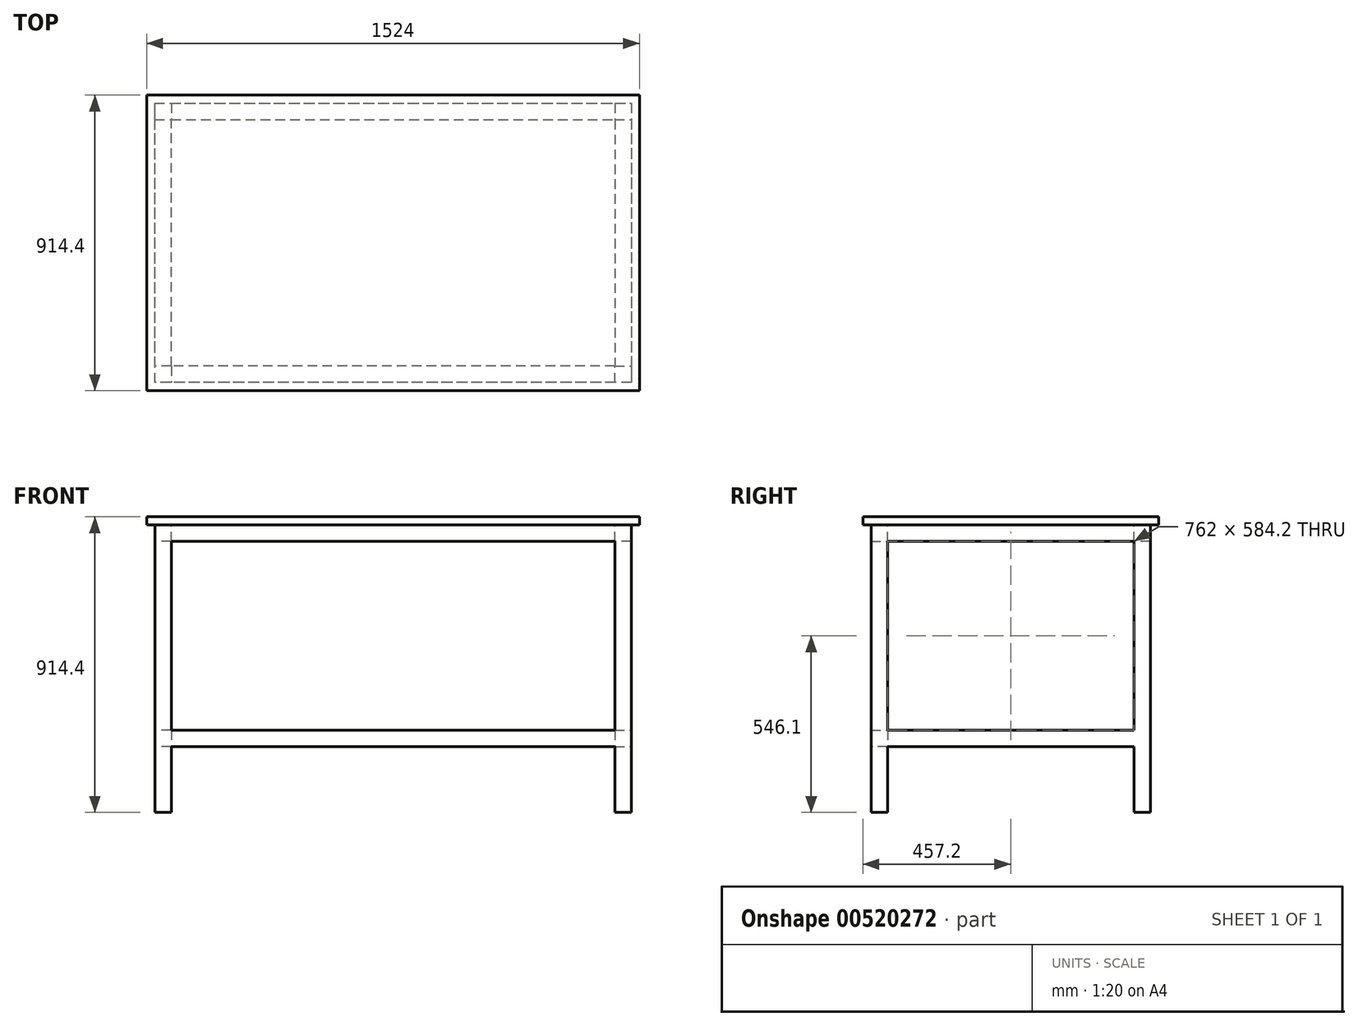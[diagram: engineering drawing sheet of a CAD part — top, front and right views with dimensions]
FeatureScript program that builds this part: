
annotation { "Feature Type Name" : "Feature", "Feature Type Description" : "" }
export const myFeature = defineFeature(function(context is Context, id is Id, definition is map)
    precondition{}
    {
        {
            var Q0;
            Q0=qCreatedBy(makeId("Top.planeOp"),FACE);
            var sketch = newSketch(context, id + "F0", { "sketchPlane" : qUnion([Q0])});
            skLineSegment(sketch, "E0.bottom", {"start": v(762, 457.2) * mm, "end": v(-762, 457.2) * mm});
            skLineSegment(sketch, "E0.top", {"start": v(762, -457.2) * mm, "end": v(-762, -457.2) * mm});
            skLineSegment(sketch, "E0.left", {"start": v(762, 457.2) * mm, "end": v(762, -457.2) * mm});
            skLineSegment(sketch, "E0.right", {"start": v(-762, 457.2) * mm, "end": v(-762, -457.2) * mm});
            skPoint(sketch, "E0.middle", {"position": v(0, 0) * mm});
            skSolve(sketch);
        }
        {
            var Q0;
            Q0 = qSketchRegion(id + "F0", true);
            extrude(context, id + "F1", {"entities" : qUnion([Q0]), "depth" : -25.4 * mm, "offsetDistance" : 25.4 * mm});
        }
        {
            var Q0;
            Q0=makeQuery(id+"F1.opExtrude","CAP_FACE",FACE,{"disambiguationData":[OSD([sQuery(id+"F0.wireOp",EDGE,"E0.bottom"),sQuery(id+"F0.wireOp",EDGE,"E0.top"),sQuery(id+"F0.wireOp",EDGE,"E0.left"),sQuery(id+"F0.wireOp",EDGE,"E0.right")])],"isStart":false});
            var sketch = newSketch(context, id + "F2", { "sketchPlane" : qUnion([Q0])});
            skLineSegment(sketch, "E1.0", {"start": v(736.6, 431.8) * mm, "end": v(-736.6, 431.8) * mm});
            skLineSegment(sketch, "E1.1", {"start": v(736.6, -431.8) * mm, "end": v(736.6, 431.8) * mm});
            skLineSegment(sketch, "E1.2", {"start": v(-736.6, -431.8) * mm, "end": v(736.6, -431.8) * mm});
            skLineSegment(sketch, "E1.3", {"start": v(-736.6, 431.8) * mm, "end": v(-736.6, -431.8) * mm});
            skLineSegment(sketch, "E2.0", {"start": v(685.8, 381) * mm, "end": v(-685.8, 381) * mm});
            skLineSegment(sketch, "E2.1", {"start": v(685.8, -381) * mm, "end": v(685.8, 381) * mm});
            skLineSegment(sketch, "E2.2", {"start": v(-685.8, -381) * mm, "end": v(685.8, -381) * mm});
            skLineSegment(sketch, "E2.3", {"start": v(-685.8, 381) * mm, "end": v(-685.8, -381) * mm});
            skSolve(sketch);
        }
        {
            var Q0;
            Q0=makeQuery(id+"F2.imprint","IMPRINT",FACE,{"disambiguationData":[TD([[makeQuery(id+"F2.imprint","IMPRINT",EDGE,{"derivedFrom":sQuery(id+"F2.wireOp",EDGE,"E1.0")}),1.0]])]});
            extrude(context, id + "F3", {"entities" : qUnion([Q0]), "operationType" : NewBodyOperationType.ADD, "depth" : 50.8 * mm, "offsetDistance" : 25.4 * mm});
        }
        {
            var Q0;
            Q0=makeQuery(id+"F3.opExtrude","CAP_FACE",FACE,{"disambiguationData":[OSD([sQuery(id+"F2.wireOp",EDGE,"E1.0"),sQuery(id+"F2.wireOp",EDGE,"E1.1"),sQuery(id+"F2.wireOp",EDGE,"E1.2"),sQuery(id+"F2.wireOp",EDGE,"E1.3"),sQuery(id+"F2.wireOp",EDGE,"E2.0"),sQuery(id+"F2.wireOp",EDGE,"E2.1"),sQuery(id+"F2.wireOp",EDGE,"E2.2"),sQuery(id+"F2.wireOp",EDGE,"E2.3")])],"isStart":false});
            var sketch = newSketch(context, id + "F4", { "sketchPlane" : qUnion([Q0])});
            skLineSegment(sketch, "E3.bottom", {"start": v(736.6, 431.8) * mm, "end": v(685.8, 431.8) * mm});
            skLineSegment(sketch, "E3.top", {"start": v(736.6, 381) * mm, "end": v(685.8, 381) * mm});
            skLineSegment(sketch, "E3.left", {"start": v(736.6, 431.8) * mm, "end": v(736.6, 381) * mm});
            skLineSegment(sketch, "E3.right", {"start": v(685.8, 431.8) * mm, "end": v(685.8, 381) * mm});
            skLineSegment(sketch, "E4.bottom", {"start": v(736.6, -431.8) * mm, "end": v(685.8, -431.8) * mm});
            skLineSegment(sketch, "E4.top", {"start": v(736.6, -381) * mm, "end": v(685.8, -381) * mm});
            skLineSegment(sketch, "E4.left", {"start": v(736.6, -431.8) * mm, "end": v(736.6, -381) * mm});
            skLineSegment(sketch, "E4.right", {"start": v(685.8, -431.8) * mm, "end": v(685.8, -381) * mm});
            skLineSegment(sketch, "E5.bottom", {"start": v(-736.6, -431.8) * mm, "end": v(-685.8, -431.8) * mm});
            skLineSegment(sketch, "E5.top", {"start": v(-736.6, -381) * mm, "end": v(-685.8, -381) * mm});
            skLineSegment(sketch, "E5.left", {"start": v(-736.6, -431.8) * mm, "end": v(-736.6, -381) * mm});
            skLineSegment(sketch, "E5.right", {"start": v(-685.8, -431.8) * mm, "end": v(-685.8, -381) * mm});
            skLineSegment(sketch, "E6.bottom", {"start": v(-685.8, 381) * mm, "end": v(-736.6, 381) * mm});
            skLineSegment(sketch, "E6.top", {"start": v(-685.8, 431.8) * mm, "end": v(-736.6, 431.8) * mm});
            skLineSegment(sketch, "E6.left", {"start": v(-685.8, 381) * mm, "end": v(-685.8, 431.8) * mm});
            skLineSegment(sketch, "E6.right", {"start": v(-736.6, 381) * mm, "end": v(-736.6, 431.8) * mm});
            skSolve(sketch);
        }
        {
            var Q0;
            Q0 = qSketchRegion(id + "F4", true);
            extrude(context, id + "F5", {"entities" : qUnion([Q0]), "operationType" : NewBodyOperationType.ADD, "depth" : 838.2 * mm, "offsetDistance" : 25.4 * mm});
        }
        {
            var Q0;
            Q0=makeQuery(id+"F5.opExtrude","SWEPT_FACE",FACE,{"disambiguationData":[OSD([sQuery(id+"F4.wireOp",EDGE,"E6.left")])]});
            var sketch = newSketch(context, id + "F6", { "sketchPlane" : qUnion([Q0])});
            skLineSegment(sketch, "E7.0", {"start": v(-381, -711.2) * mm, "end": v(-431.8, -711.2) * mm});
            skLineSegment(sketch, "E8.bottom", {"start": v(-431.8, -711.2) * mm, "end": v(-381, -711.2) * mm});
            skLineSegment(sketch, "E8.top", {"start": v(-431.8, -660.4) * mm, "end": v(-381, -660.4) * mm});
            skLineSegment(sketch, "E8.left", {"start": v(-431.8, -711.2) * mm, "end": v(-431.8, -660.4) * mm});
            skLineSegment(sketch, "E8.right", {"start": v(-381, -711.2) * mm, "end": v(-381, -660.4) * mm});
            skSolve(sketch);
        }
        {
            var Q0;
            Q0 = qSketchRegion(id + "F6", true);
            extrude(context, id + "F7", {"entities" : qUnion([Q0]), "operationType" : NewBodyOperationType.ADD, "endBound" : BoundingType.UP_TO_NEXT, "depth" : 25.4 * mm, "offsetDistance" : 25.4 * mm});
        }
        {
            var Q0;
            Q0=makeQuery(id+"F7.boolean.opBoolean","MERGE",FACE,{"derivedFrom":[makeQuery(id+"F5.opExtrude","SWEPT_FACE",FACE,{"disambiguationData":[OSD([sQuery(id+"F4.wireOp",EDGE,"E3.top")])]}),makeQuery(id+"F5.opExtrude","SWEPT_FACE",FACE,{"disambiguationData":[OSD([sQuery(id+"F4.wireOp",EDGE,"E6.bottom")])]}),makeQuery(id+"F7.opExtrude","SWEPT_FACE",FACE,{"disambiguationData":[OSD([sQuery(id+"F6.wireOp",EDGE,"E8.right")])]})]});
            var sketch = newSketch(context, id + "F8", { "sketchPlane" : qUnion([Q0])});
            skLineSegment(sketch, "E9.bottom", {"start": v(-685.8, -660.4) * mm, "end": v(-736.6, -660.4) * mm});
            skLineSegment(sketch, "E9.top", {"start": v(-685.8, -711.2) * mm, "end": v(-736.6, -711.2) * mm});
            skLineSegment(sketch, "E9.left", {"start": v(-685.8, -660.4) * mm, "end": v(-685.8, -711.2) * mm});
            skLineSegment(sketch, "E9.right", {"start": v(-736.6, -660.4) * mm, "end": v(-736.6, -711.2) * mm});
            skLineSegment(sketch, "E10.bottom", {"start": v(685.8, -660.4) * mm, "end": v(736.6, -660.4) * mm});
            skLineSegment(sketch, "E10.top", {"start": v(685.8, -711.2) * mm, "end": v(736.6, -711.2) * mm});
            skLineSegment(sketch, "E10.left", {"start": v(685.8, -660.4) * mm, "end": v(685.8, -711.2) * mm});
            skLineSegment(sketch, "E10.right", {"start": v(736.6, -660.4) * mm, "end": v(736.6, -711.2) * mm});
            skSolve(sketch);
        }
        {
            var Q0;
            Q0 = qSketchRegion(id + "F8", true);
            extrude(context, id + "F9", {"entities" : qUnion([Q0]), "operationType" : NewBodyOperationType.ADD, "endBound" : BoundingType.UP_TO_NEXT, "depth" : 25.4 * mm, "offsetDistance" : 25.4 * mm});
        }
    });
